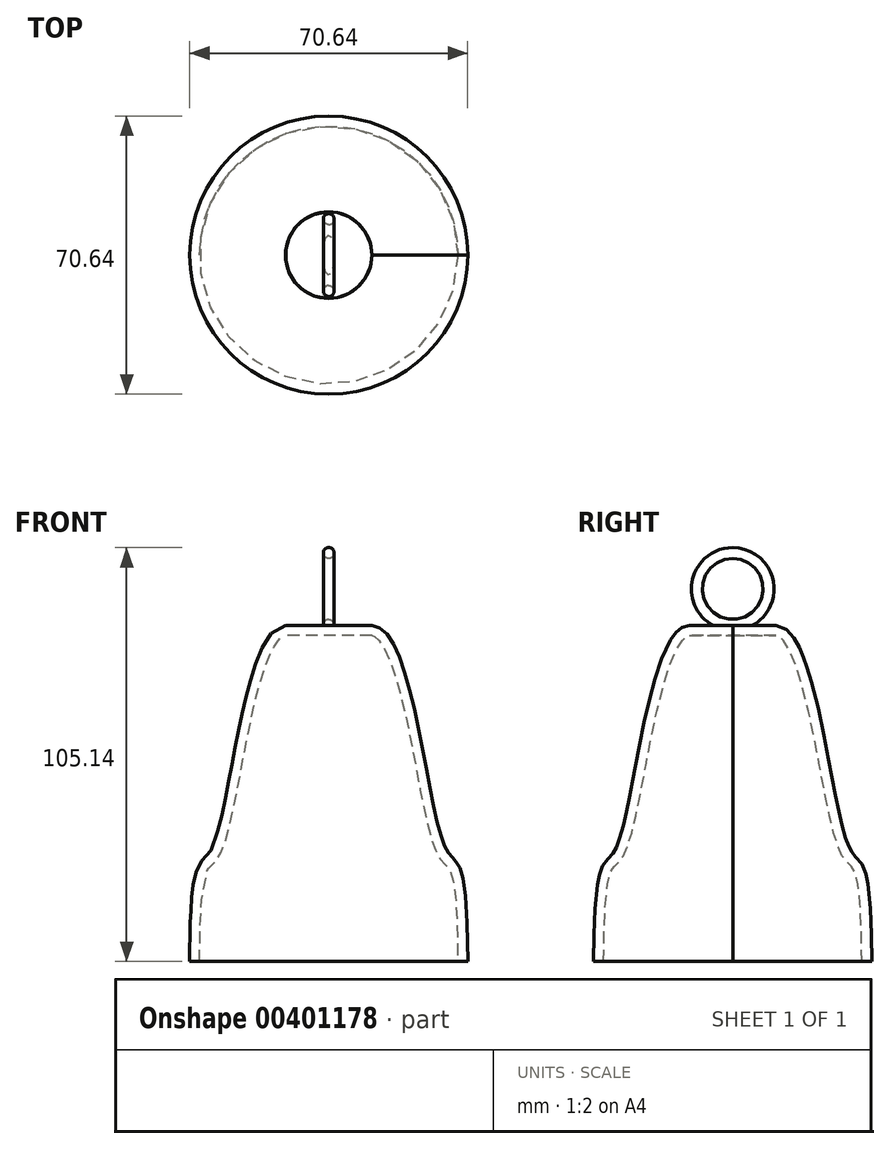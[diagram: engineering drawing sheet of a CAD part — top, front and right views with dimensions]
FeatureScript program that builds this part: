
annotation { "Feature Type Name" : "Feature", "Feature Type Description" : "" }
export const myFeature = defineFeature(function(context is Context, id is Id, definition is map)
    precondition{}
    {
        {
            var Q0;
            Q0=qCreatedBy(makeId("Top.planeOp"),FACE);
            cPlane(context, id + "F0", {"entities" : qUnion([Q0]), "cplaneType" : CPlaneType.OFFSET, "offset" : 85.34 * mm, "width" : 152.4 * mm, "height" : 152.4 * mm});
        }
        {
            var Q0;
            Q0=qCreatedBy(id+"F0.planeOp",FACE);
            var sketch = newSketch(context, id + "F1", { "sketchPlane" : qUnion([Q0])});
            skCircle(sketch, "E0", {"center": v(0, 0) * mm, "radius": 10.98 * mm});
            skSolve(sketch);
        }
        {
            var Q0;
            Q0=qCreatedBy(makeId("Top.planeOp"),FACE);
            var sketch = newSketch(context, id + "F2", { "sketchPlane" : qUnion([Q0])});
            skCircle(sketch, "E1", {"center": v(0, 0) * mm, "radius": 35.32 * mm});
            skSolve(sketch);
        }
        {
            var Q0;
            Q0=qCreatedBy(makeId("Top.planeOp"),FACE);
            cPlane(context, id + "F3", {"entities" : qUnion([Q0]), "cplaneType" : CPlaneType.OFFSET, "offset" : 28.2 * mm, "width" : 152.4 * mm, "height" : 152.4 * mm});
        }
        {
            var Q0;
            Q0=qCreatedBy(id+"F3.planeOp",FACE);
            var sketch = newSketch(context, id + "F4", { "sketchPlane" : qUnion([Q0])});
            skCircle(sketch, "E2", {"center": v(0, 0) * mm, "radius": 29.97 * mm});
            skSolve(sketch);
        }
        {
            var Q0;
            Q0=makeQuery(id+"F1.imprint","IMPRINT",FACE,{"disambiguationData":[TD([[makeQuery(id+"F1.imprint","IMPRINT",EDGE,{"derivedFrom":sQuery(id+"F1.wireOp",EDGE,"E0")}),1.0]])]});
            var Q1;
            Q1=makeQuery(id+"F4.imprint","IMPRINT",FACE,{"disambiguationData":[TD([[makeQuery(id+"F4.imprint","IMPRINT",EDGE,{"derivedFrom":sQuery(id+"F4.wireOp",EDGE,"E2")}),1.0]])]});
            var Q2;
            Q2=makeQuery(id+"F2.imprint","IMPRINT",FACE,{"disambiguationData":[TD([[makeQuery(id+"F2.imprint","IMPRINT",EDGE,{"derivedFrom":sQuery(id+"F2.wireOp",EDGE,"E1")}),1.0]])]});
            loft(context, id + "F5", {"startCondition" : LoftEndDerivativeType.TANGENT_TO_PROFILE, "startMagnitude" : 1.5, "endCondition" : LoftEndDerivativeType.NORMAL_TO_PROFILE, "endMagnitude" : 3, "sheetProfilesArray" : [{ "sheetProfileEntities" : qUnion([Q0]) }, { "sheetProfileEntities" : qUnion([Q1]) }, { "sheetProfileEntities" : qUnion([Q2]) }]});
        }
        {
            var Q0;
            Q0=makeQuery(id+"F5.opLoft","CAP_FACE",FACE,{"disambiguationData":[OSD([makeQuery(id+"F2.imprint","IMPRINT",FACE,{"disambiguationData":[TD([[makeQuery(id+"F2.imprint","IMPRINT",EDGE,{"derivedFrom":sQuery(id+"F2.wireOp",EDGE,"E1")}),1.0]])]})])],"isStart":true});
            shell(context, id + "F6", {"entities" : qUnion([Q0]), "thickness" : 2.54 * mm});
        }
        {
            var Q0;
            Q0=makeQuery(id+"F5.opLoft","CAP_FACE",FACE,{"disambiguationData":[OSD([makeQuery(id+"F1.imprint","IMPRINT",FACE,{"disambiguationData":[TD([[makeQuery(id+"F1.imprint","IMPRINT",EDGE,{"derivedFrom":sQuery(id+"F1.wireOp",EDGE,"E0")}),1.0]])]})])],"isStart":true});
            var sketch = newSketch(context, id + "F7", { "sketchPlane" : qUnion([Q0])});
            skPoint(sketch, "E3", {"position": v(0, 0) * mm});
            skSolve(sketch);
        }
        {
            var Q0;
            Q0=qCreatedBy(makeId("Right.planeOp"),FACE);
            var sketch = newSketch(context, id + "F8", { "sketchPlane" : qUnion([Q0])});
            skCircle(sketch, "E4", {"center": v(0, 94.63) * mm, "radius": 9.12 * mm});
            skSolve(sketch);
        }
        {
            var Q0;
            Q0=sQuery(id+"F8.wireOp",EDGE,"E4");
            var Q1;
            Q1=sQuery(id+"F7.wireOp",VERTEX,"E3");
            cPlane(context, id + "F9", {"entities" : qUnion([Q0, Q1]), "cplaneType" : CPlaneType.CURVE_POINT, "offset" : 25.4 * mm, "width" : 152.4 * mm, "height" : 152.4 * mm});
        }
        {
            var Q0;
            Q0=qCreatedBy(id+"F9.planeOp",FACE);
            var sketch = newSketch(context, id + "F10", { "sketchPlane" : qUnion([Q0])});
            skCircle(sketch, "E5", {"center": v(0, 85.5) * mm, "radius": 1.38 * mm});
            skSolve(sketch);
        }
        {
            var Q0;
            Q0 = qSketchRegion(id + "F10", true);
            var Q1;
            Q1 = qConstructionFilter(qBodyType(qCreatedBy(id + "F8" ,EDGE), BodyType.WIRE), ConstructionObject.NO);
            sweep(context, id + "F11", {"operationType" : NewBodyOperationType.ADD, "profiles" : qUnion([Q0]), "path" : qUnion([Q1])});
        }
    });
